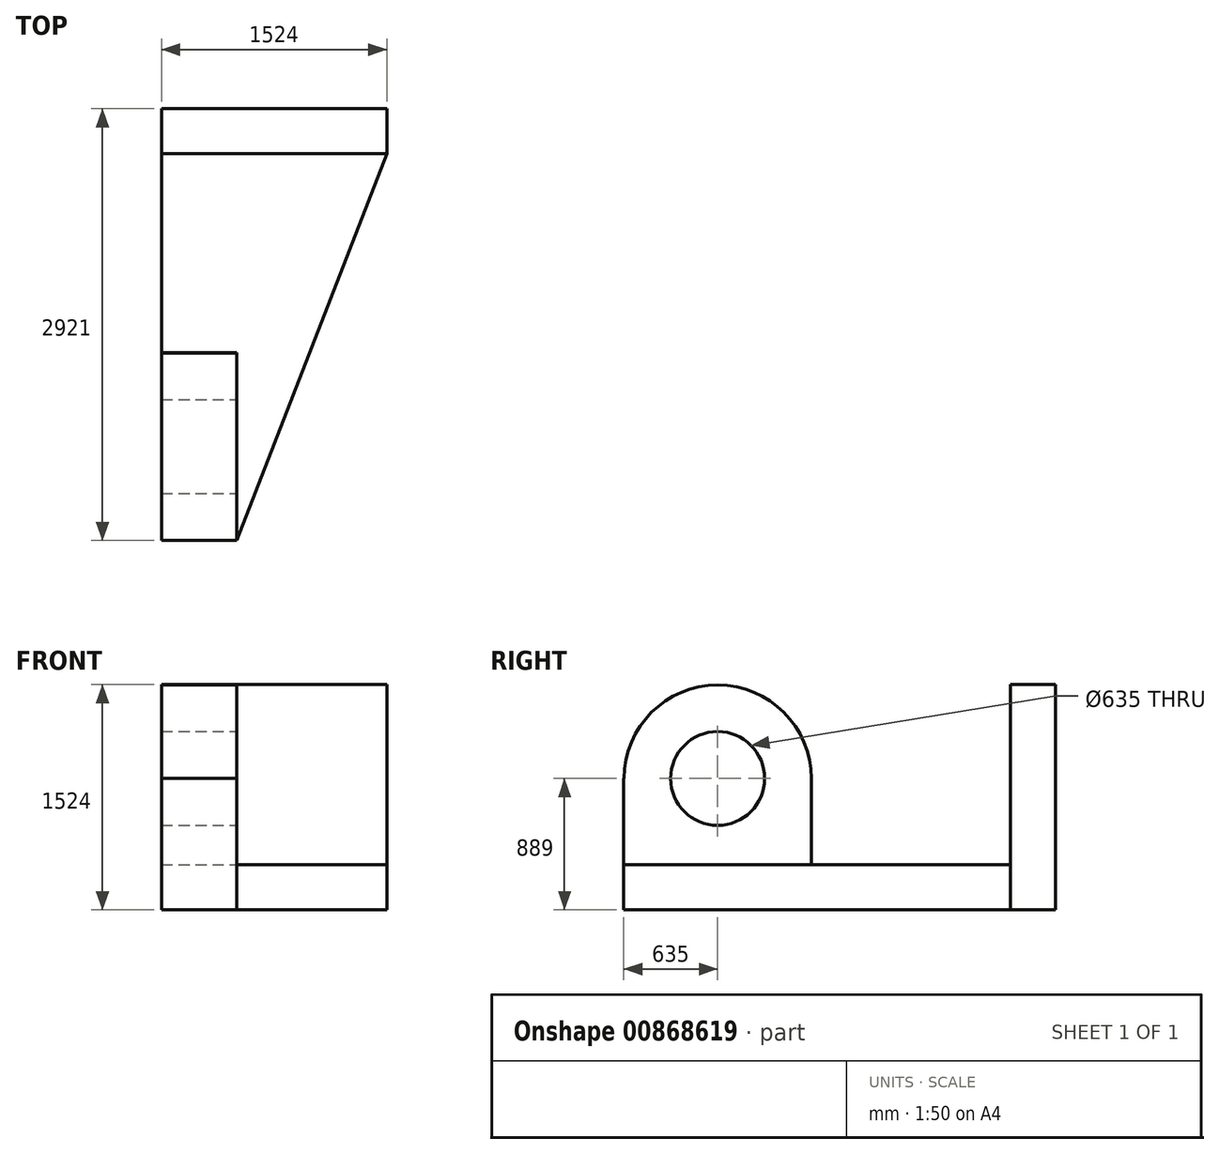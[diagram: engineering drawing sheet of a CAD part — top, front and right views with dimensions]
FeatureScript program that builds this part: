
annotation { "Feature Type Name" : "Feature", "Feature Type Description" : "" }
export const myFeature = defineFeature(function(context is Context, id is Id, definition is map)
    precondition{}
    {
        {
            var Q0;
            Q0=qCreatedBy(makeId("Front.planeOp"),FACE);
            var sketch = newSketch(context, id + "F0", { "sketchPlane" : qUnion([Q0])});
            skLineSegment(sketch, "E0.bottom", {"start": v(-153.83, -85.8) * mm, "end": v(1370.17, -85.8) * mm});
            skLineSegment(sketch, "E0.top", {"start": v(-153.83, 1438.2) * mm, "end": v(1370.17, 1438.2) * mm});
            skLineSegment(sketch, "E0.left", {"start": v(-153.83, -85.8) * mm, "end": v(-153.83, 1438.2) * mm});
            skLineSegment(sketch, "E0.right", {"start": v(1370.17, -85.8) * mm, "end": v(1370.17, 1438.2) * mm});
            skSolve(sketch);
        }
        {
            var Q0;
            Q0=makeQuery(id+"F0.imprint","IMPRINT",FACE,{"disambiguationData":[TD([[makeQuery(id+"F0.imprint","IMPRINT",EDGE,{"derivedFrom":sQuery(id+"F0.wireOp",EDGE,"E0.bottom")}),1.0]])]});
            extrude(context, id + "F1", {"entities" : qUnion([Q0]), "depth" : 304.8 * mm, "offsetDistance" : 25.4 * mm});
        }
        {
            var Q0;
            Q0=makeQuery(id+"F1.opExtrude","CAP_FACE",FACE,{"disambiguationData":[OSD([sQuery(id+"F0.wireOp",EDGE,"E0.bottom"),sQuery(id+"F0.wireOp",EDGE,"E0.top"),sQuery(id+"F0.wireOp",EDGE,"E0.left"),sQuery(id+"F0.wireOp",EDGE,"E0.right")])],"isStart":false});
            var sketch = newSketch(context, id + "F2", { "sketchPlane" : qUnion([Q0])});
            skLineSegment(sketch, "E1.bottom", {"start": v(-153.83, -85.8) * mm, "end": v(1370.17, -85.8) * mm});
            skLineSegment(sketch, "E1.top", {"start": v(-153.83, 219) * mm, "end": v(1370.17, 219) * mm});
            skLineSegment(sketch, "E1.left", {"start": v(-153.83, -85.8) * mm, "end": v(-153.83, 219) * mm});
            skLineSegment(sketch, "E1.right", {"start": v(1370.17, -85.8) * mm, "end": v(1370.17, 219) * mm});
            skSolve(sketch);
        }
        {
            var Q0;
            Q0=makeQuery(id+"F2.imprint","IMPRINT",FACE,{"disambiguationData":[TD([[makeQuery(id+"F2.imprint","IMPRINT",EDGE,{"derivedFrom":sQuery(id+"F2.wireOp",EDGE,"E1.bottom")}),1.0]])]});
            extrude(context, id + "F3", {"entities" : qUnion([Q0]), "operationType" : NewBodyOperationType.ADD, "depth" : 2616.2 * mm, "offsetDistance" : 25.4 * mm});
        }
        {
            var Q0;
            Q0=makeQuery(id+"F3.opExtrude","SWEPT_FACE",FACE,{"disambiguationData":[OSD([sQuery(id+"F2.wireOp",EDGE,"E1.top")])]});
            var sketch = newSketch(context, id + "F4", { "sketchPlane" : qUnion([Q0])});
            skLineSegment(sketch, "E2.bottom", {"start": v(-153.83, -2921) * mm, "end": v(354.17, -2921) * mm});
            skLineSegment(sketch, "E2.top", {"start": v(-153.83, -1651) * mm, "end": v(354.17, -1651) * mm});
            skLineSegment(sketch, "E2.left", {"start": v(-153.83, -2921) * mm, "end": v(-153.83, -1651) * mm});
            skLineSegment(sketch, "E2.right", {"start": v(354.17, -2921) * mm, "end": v(354.17, -1651) * mm});
            skSolve(sketch);
        }
        {
            var Q0;
            Q0=makeQuery(id+"F4.imprint","IMPRINT",FACE,{"disambiguationData":[TD([[makeQuery(id+"F4.imprint","IMPRINT",EDGE,{"derivedFrom":sQuery(id+"F4.wireOp",EDGE,"E2.bottom")}),1.0]])]});
            extrude(context, id + "F5", {"entities" : qUnion([Q0]), "operationType" : NewBodyOperationType.ADD, "depth" : 584.2 * mm, "offsetDistance" : 25.4 * mm});
        }
        {
            var Q0;
            Q0=makeQuery(id+"F5.opExtrude","SWEPT_FACE",FACE,{"disambiguationData":[OSD([sQuery(id+"F4.wireOp",EDGE,"E2.right")])]});
            var sketch = newSketch(context, id + "F6", { "sketchPlane" : qUnion([Q0])});
            skCircle(sketch, "E3", {"center": v(-2286, 803.2) * mm, "radius": 632.62 * mm});
            skSolve(sketch);
        }
        {
            var Q0;
            {var subQ0=sQuery(id+"F6.wireOp",EDGE,"E3");var subQ1=makeQuery(id+"F5.opExtrude","CAP_EDGE",EDGE,{"disambiguationData":[OSD([sQuery(id+"F4.wireOp",EDGE,"E2.right")])],"isStart":false});var subQ2=makeQuery(id+"F6.imprint","INTERSECT",VERTEX,{"disambiguationData":[OD(0.0)],"derivedFrom":[subQ1,subQ0]});Q0=makeQuery(id+"F6.imprint","IMPRINT",FACE,{"disambiguationData":[TD([[makeQuery(id+"F6.imprint","IMPRINT",EDGE,{"disambiguationData":[TD([[subQ2,1.0]])],"derivedFrom":subQ0}),1.0]])]});}
            extrude(context, id + "F7", {"entities" : qUnion([Q0]), "operationType" : NewBodyOperationType.ADD, "oppositeDirection" : true, "depth" : 508 * mm, "offsetDistance" : 25.4 * mm});
        }
        {
            var Q0;
            {var subQ0=sQuery(id+"F4.wireOp",EDGE,"E2.right");Q0=makeQuery(id+"F7.boolean.opBoolean","MERGE",FACE,{"derivedFrom":[makeQuery(id+"F5.opExtrude","SWEPT_FACE",FACE,{"disambiguationData":[OSD([subQ0])]}),makeQuery(id+"F7.opExtrude","CAP_FACE",FACE,{"disambiguationData":[OSD([subQ0,sQuery(id+"F6.wireOp",EDGE,"E3")])],"isStart":true})]});}
            var sketch = newSketch(context, id + "F8", { "sketchPlane" : qUnion([Q0])});
            skCircle(sketch, "E4", {"center": v(-2286, 803.2) * mm, "radius": 317.5 * mm});
            skSolve(sketch);
        }
        {
            var Q0;
            Q0=makeQuery(id+"F8.imprint","IMPRINT",FACE,{"disambiguationData":[TD([[makeQuery(id+"F8.imprint","IMPRINT",EDGE,{"derivedFrom":sQuery(id+"F8.wireOp",EDGE,"E4")}),1.0]])]});
            var sketch = newSketch(context, id + "F9", { "sketchPlane" : qUnion([Q0])});
            skSolve(sketch);
        }
        {
            var Q0;
            Q0=makeQuery(id+"F9.imprint","IMPRINT",FACE,{"disambiguationData":[TD([[makeQuery(id+"F9.imprint","IMPRINT",EDGE,{"derivedFrom":makeQuery(id+"F8.imprint","IMPRINT",EDGE,{"derivedFrom":sQuery(id+"F8.wireOp",EDGE,"E4")})}),1.0]])]});
            var sketch = newSketch(context, id + "F10", { "sketchPlane" : qUnion([Q0])});
            skSolve(sketch);
        }
        {
            var Q0;
            Q0 = qSketchRegion(id + "F10", true);
            var Q1;
            Q1=makeQuery(id+"F10.imprint","IMPRINT",FACE,{"disambiguationData":[TD([[makeQuery(id+"F10.imprint","IMPRINT",EDGE,{"derivedFrom":makeQuery(id+"F9.imprint","IMPRINT",EDGE,{"derivedFrom":makeQuery(id+"F8.imprint","IMPRINT",EDGE,{"derivedFrom":sQuery(id+"F8.wireOp",EDGE,"E4")})})}),1.0]])]});
            extrude(context, id + "F11", {"entities" : qUnion([Q0, Q1]), "operationType" : NewBodyOperationType.REMOVE, "oppositeDirection" : true, "depth" : 1231.9 * mm, "offsetDistance" : 25.4 * mm});
        }
        {
            var Q0;
            Q0=makeQuery(id+"F3.opExtrude","SWEPT_FACE",FACE,{"disambiguationData":[OSD([sQuery(id+"F2.wireOp",EDGE,"E1.top")])]});
            var sketch = newSketch(context, id + "F12", { "sketchPlane" : qUnion([Q0])});
            skLineSegment(sketch, "E5", {"start": v(354.17, -2921) * mm, "end": v(1370.17, -304.8) * mm});
            skLineSegment(sketch, "E6", {"start": v(1370.17, -304.8) * mm, "end": v(1370.17, -2921) * mm});
            skLineSegment(sketch, "E7", {"start": v(1370.17, -2921) * mm, "end": v(354.17, -2921) * mm});
            skSolve(sketch);
        }
        {
            var Q0;
            Q0=makeQuery(id+"F12.imprint","IMPRINT",FACE,{"disambiguationData":[TD([[makeQuery(id+"F12.imprint","IMPRINT",EDGE,{"derivedFrom":sQuery(id+"F12.wireOp",EDGE,"E5")}),-1.0]])]});
            var sketch = newSketch(context, id + "F13", { "sketchPlane" : qUnion([Q0])});
            skSolve(sketch);
        }
        {
            var Q0;
            Q0 = qSketchRegion(id + "F13", true);
            var Q1;
            Q1=makeQuery(id+"F12.imprint","IMPRINT",FACE,{"disambiguationData":[TD([[makeQuery(id+"F12.imprint","IMPRINT",EDGE,{"derivedFrom":sQuery(id+"F12.wireOp",EDGE,"E5")}),-1.0]])]});
            extrude(context, id + "F14", {"entities" : qUnion([Q0, Q1]), "operationType" : NewBodyOperationType.REMOVE, "oppositeDirection" : true, "depth" : 1102.36 * mm, "offsetDistance" : 25.4 * mm});
        }
    });
